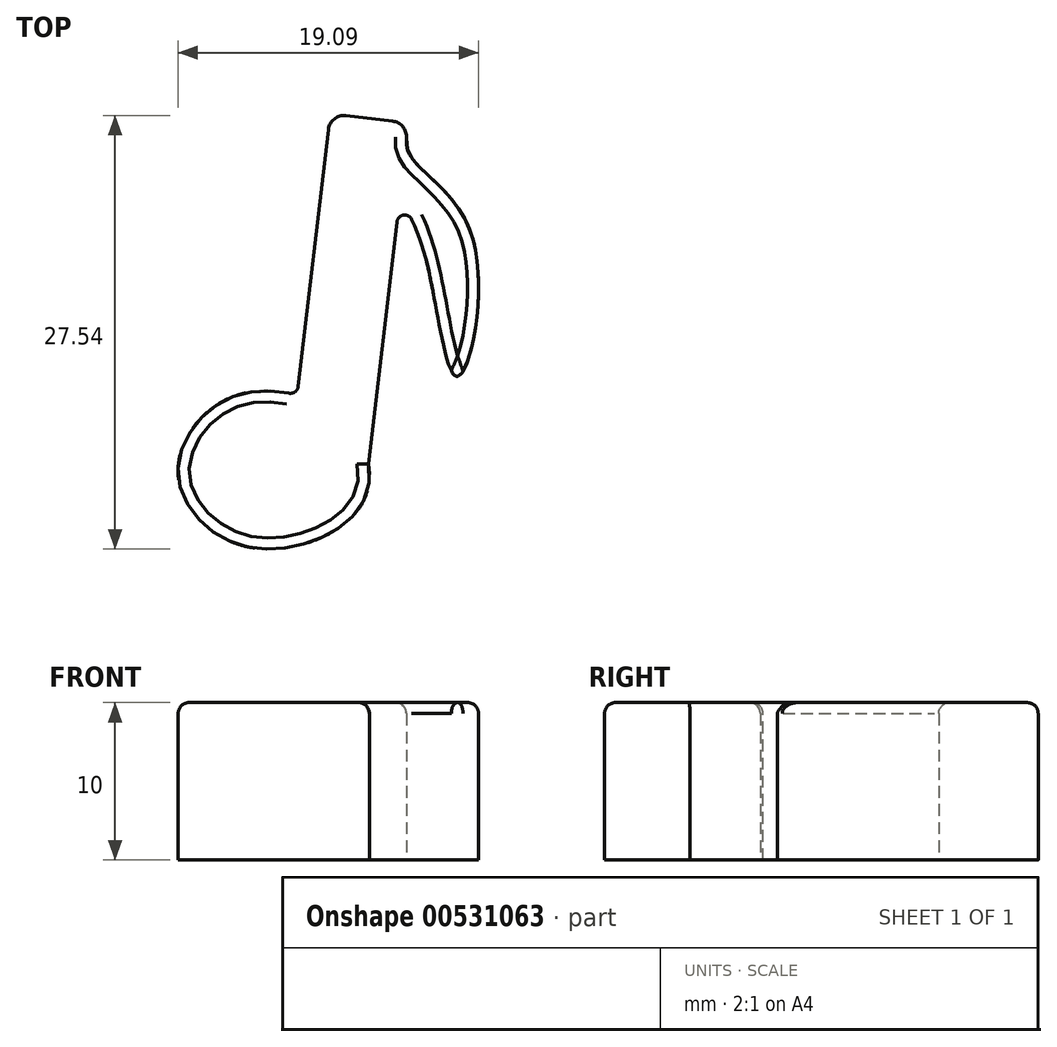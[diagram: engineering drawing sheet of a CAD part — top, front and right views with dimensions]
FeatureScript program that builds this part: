
annotation { "Feature Type Name" : "Feature", "Feature Type Description" : "" }
export const myFeature = defineFeature(function(context is Context, id is Id, definition is map)
    precondition{}
    {
        {
            var Q0;
            Q0=qCreatedBy(makeId("Top.planeOp"),FACE);
            var sketch = newSketch(context, id + "F0", { "sketchPlane" : qUnion([Q0])});
            skPoint(sketch, "E0", {"position": v(-9.37, -4.65) * mm});
            skPoint(sketch, "E1", {"position": v(-13.83, 0) * mm});
            skPoint(sketch, "E2", {"position": v(-3.03, 3.08) * mm});
            skPoint(sketch, "E3", {"position": v(-10.06, 5) * mm});
            skPoint(sketch, "E4", {"position": v(-2.23, -2.02) * mm});
            skFitSpline(sketch, "E5", {"points": [v(-13.83, 0) * mm, v(-9.37, -4.65) * mm, v(-2.23, -2.02) * mm, v(-3.03, 3.08) * mm, v(-10.06, 5) * mm, v(-13.83, 0) * mm]});
            skLineSegment(sketch, "E6", {"start": v(-6.2, 5.55) * mm, "end": v(-4.29, 21.88) * mm});
            skLineSegment(sketch, "E7", {"start": v(-1.75, 0.63) * mm, "end": v(0.06, 16) * mm});
            skLineSegment(sketch, "E8", {"start": v(-3.18, 22.75) * mm, "end": v(-0.21, 22.4) * mm});
            skFitSpline(sketch, "E9", {"points": [v(0.8, 22.29) * mm, v(0.8, 20.41) * mm, v(4.83, 15.08) * mm, v(3.88, 6.2) * mm, v(1.82, 13.97) * mm, v(0.26, 17.74) * mm], "startDerivative": vector(-0.8, -13.35) * mm, "endDerivative": vector(-5.6, 15.68) * mm});
            skPoint(sketch, "E10.visualSharp", {"position": v(-4.17, 22.87) * mm});
            skArc(sketch, "E10.filletArc", {"start": v(-3.18, 22.75) * mm, "mid": v(-3.91, 22.54) * mm, "end": v(-4.29, 21.88) * mm});
            skArc(sketch, "E11.filletArc", {"start": v(0.67, 21.33) * mm, "mid": v(0.44, 22.04) * mm, "end": v(-0.21, 22.4) * mm});
            skArc(sketch, "E12.filletArc", {"start": v(1, 16.16) * mm, "mid": v(0.47, 16.44) * mm, "end": v(0.06, 16) * mm});
            skPoint(sketch, "E13.visualSharp", {"position": v(-6.27, 5) * mm});
            skArc(sketch, "E13.filletArc", {"start": v(-6.8, 5.12) * mm, "mid": v(-6.41, 5.2) * mm, "end": v(-6.2, 5.55) * mm});
            skSolve(sketch);
        }
        {
            var Q0;
            {var subQ0=sQuery(id+"F0.wireOp",EDGE,"E5");var subQ1=makeQuery(id+"F0.imprint","INTERSECT",VERTEX,{"derivedFrom":[subQ0,sQuery(id+"F0.wireOp",EDGE,"E6")]});Q0=makeQuery(id+"F0.imprint","IMPRINT",FACE,{"disambiguationData":[TD([[makeQuery(id+"F0.imprint","IMPRINT",EDGE,{"disambiguationData":[TD([[subQ1,1.0]])],"derivedFrom":subQ0}),1.0]])]});}
            var Q1;
            {var subQ1=sQuery(id+"F0.wireOp",EDGE,"E6");Q1=makeQuery(id+"F0.imprint","IMPRINT",FACE,{"disambiguationData":[TD([[makeQuery(id+"F0.imprint","IMPRINT",EDGE,{"derivedFrom":subQ1}),-1.0]])]});}
            extrude(context, id + "F1", {"entities" : qUnion([Q0, Q1]), "depth" : 10 * mm, "offsetDistance" : 25 * mm});
        }
        {
            var Q0;
            Q0=makeQuery(id+"F1.opExtrude","CAP_FACE",FACE,{"disambiguationData":[OSD([sQuery(id+"F0.wireOp",EDGE,"E5"),sQuery(id+"F0.wireOp",EDGE,"E6"),sQuery(id+"F0.wireOp",EDGE,"E7"),sQuery(id+"F0.wireOp",EDGE,"E8"),sQuery(id+"F0.wireOp",EDGE,"E9"),sQuery(id+"F0.wireOp",EDGE,"E10.filletArc"),sQuery(id+"F0.wireOp",EDGE,"E11.filletArc"),sQuery(id+"F0.wireOp",EDGE,"E12.filletArc"),sQuery(id+"F0.wireOp",EDGE,"E13.filletArc")])],"isStart":false});
            fillet(context, id + "F2", {"entities" : qUnion([Q0]), "radius" : .7 * mm, "tangentPropagation" : true, "allowEdgeOverflow" : false});
        }
    });
